# Revit family: Bench-Allermuir-Waves
name_source: partatom
category: Furniture
revit_build: Autodesk Revit Architecture 2012 (Build: 20110309_2315(x64)
units: mm (PartAtom-declared; Revit-internal decimal feet)

## types (1)
- A440
    04 CSI = 12 51 00
    95 CSI = 12510
    Assembly Code = E2020200
    Brochure URL = http://www.allermuir.net
    CAD Blocks URL = http://www.allermuir.net
    Color Availability = See price list for material options
    Fabric Spec Sheets = http://www.allermuir.net
    LEED Stats URL = http://www.allermuir.net
    Leg Support Finish = Metal - Allermuir - Upholstery - Stainless - Brushed
    Manufacturer = Allermuir
    Manufacturer Fax = (419) 887 5805
    Model = A440
    Overall Depth = 1' - 6 29/32"
    Overall Height = 1' - 5 23/32"
    Overall Width = 5' - 4 17/32"
    Plugin Data URL = http://products.ecoscorecard.com
    Pricing URL = http://www.allermuir.net
    Product Line = Waves
    Product Page URL = http://www.allermuir.net
    Seat Depth = 1' - 6 29/32"
    Seat Height = 1' - 5 23/32"
    Seat Width = 5' - 4 17/32"
    Seat or Base = Wood - Allermuir - Cherry - Stained Dark Low Gloss
    Specifications URL = http://www.allermuir.net
    Subcategory = Benches
    URL = http://www.allermuir.net
    Weight = 0.0 lb
    ecoScorecard Product Page = http://products.ecoscorecard.com
    ecoScorecard_data = http://thesenatorgroup.ecoscorecard.com

## geometry (parser evidence)
native form markers: Blend x22, Sweep x2
no freeform markers — native parametric forms only
